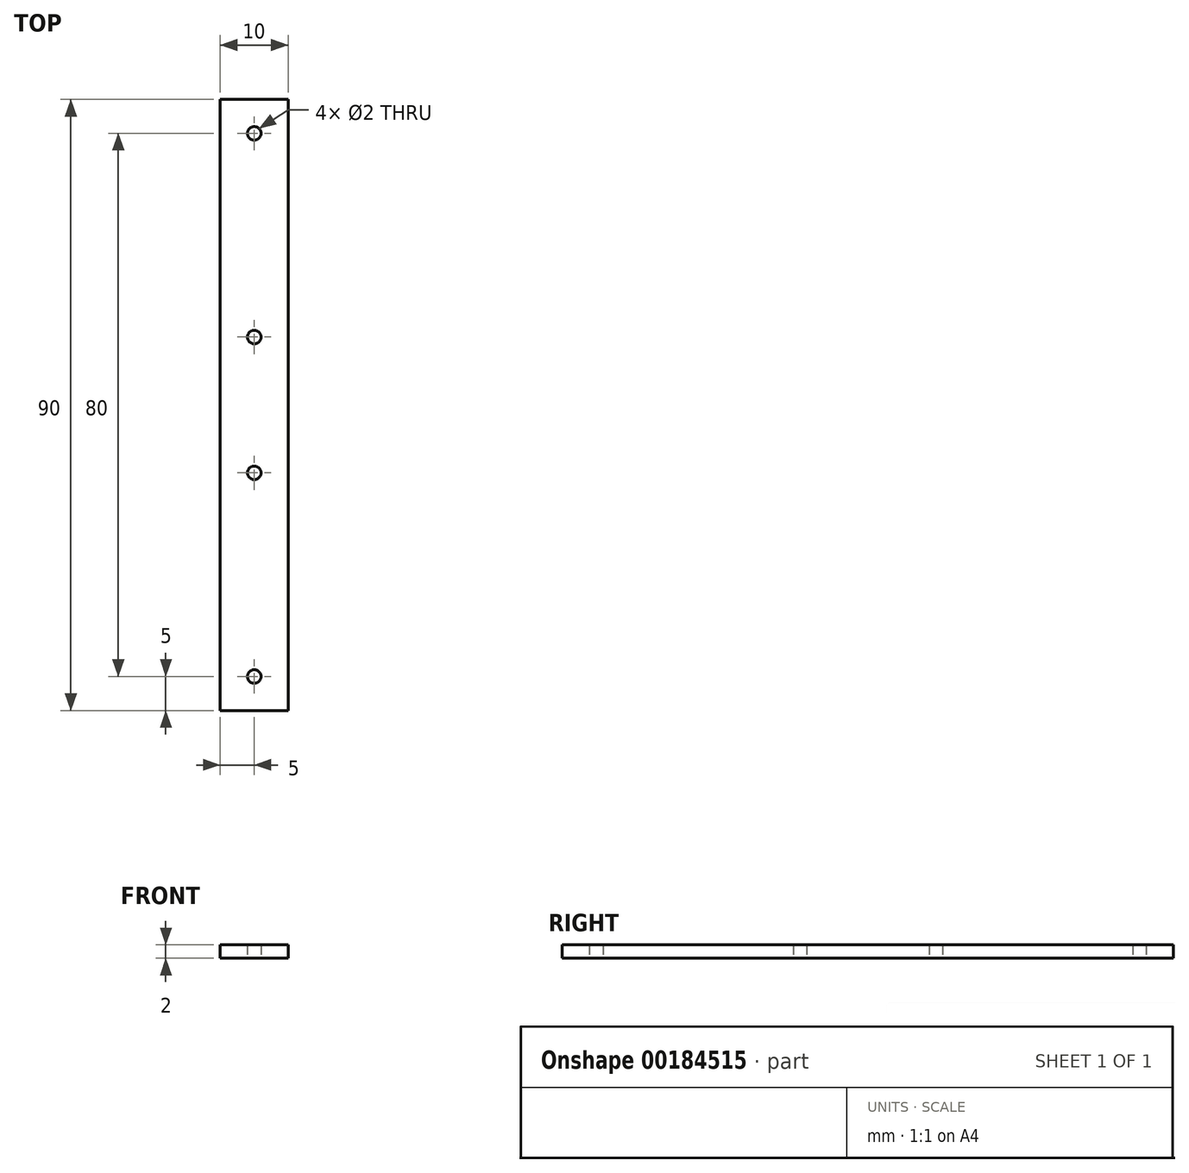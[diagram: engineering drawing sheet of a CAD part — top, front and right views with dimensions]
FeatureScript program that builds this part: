
annotation { "Feature Type Name" : "Feature", "Feature Type Description" : "" }
export const myFeature = defineFeature(function(context is Context, id is Id, definition is map)
    precondition{}
    {
        {
            var Q0;
            Q0=qCreatedBy(makeId("Top.planeOp"),FACE);
            var sketch = newSketch(context, id + "F0", { "sketchPlane" : qUnion([Q0])});
            skLineSegment(sketch, "E0.bottom", {"start": v(0, 0) * mm, "end": v(10, 0) * mm});
            skLineSegment(sketch, "E0.top", {"start": v(0, -90) * mm, "end": v(10, -90) * mm});
            skLineSegment(sketch, "E0.left", {"start": v(0, 0) * mm, "end": v(0, -90) * mm});
            skLineSegment(sketch, "E0.right", {"start": v(10, 0) * mm, "end": v(10, -90) * mm});
            skCircle(sketch, "E1", {"center": v(5, -5) * mm, "radius": 1 * mm});
            skCircle(sketch, "E2", {"center": v(5, -85) * mm, "radius": 1 * mm});
            skCircle(sketch, "E3", {"center": v(5, -35) * mm, "radius": 1 * mm});
            skCircle(sketch, "E4", {"center": v(5, -55) * mm, "radius": 1 * mm});
            skSolve(sketch);
        }
        {
            var Q0;
            Q0=makeQuery(id+"F0.imprint","IMPRINT",FACE,{"disambiguationData":[TD([[makeQuery(id+"F0.imprint","IMPRINT",EDGE,{"derivedFrom":sQuery(id+"F0.wireOp",EDGE,"E0.bottom")}),-1.0]])]});
            extrude(context, id + "F1", {"entities" : qUnion([Q0]), "depth" : 2 * mm});
        }
    });
